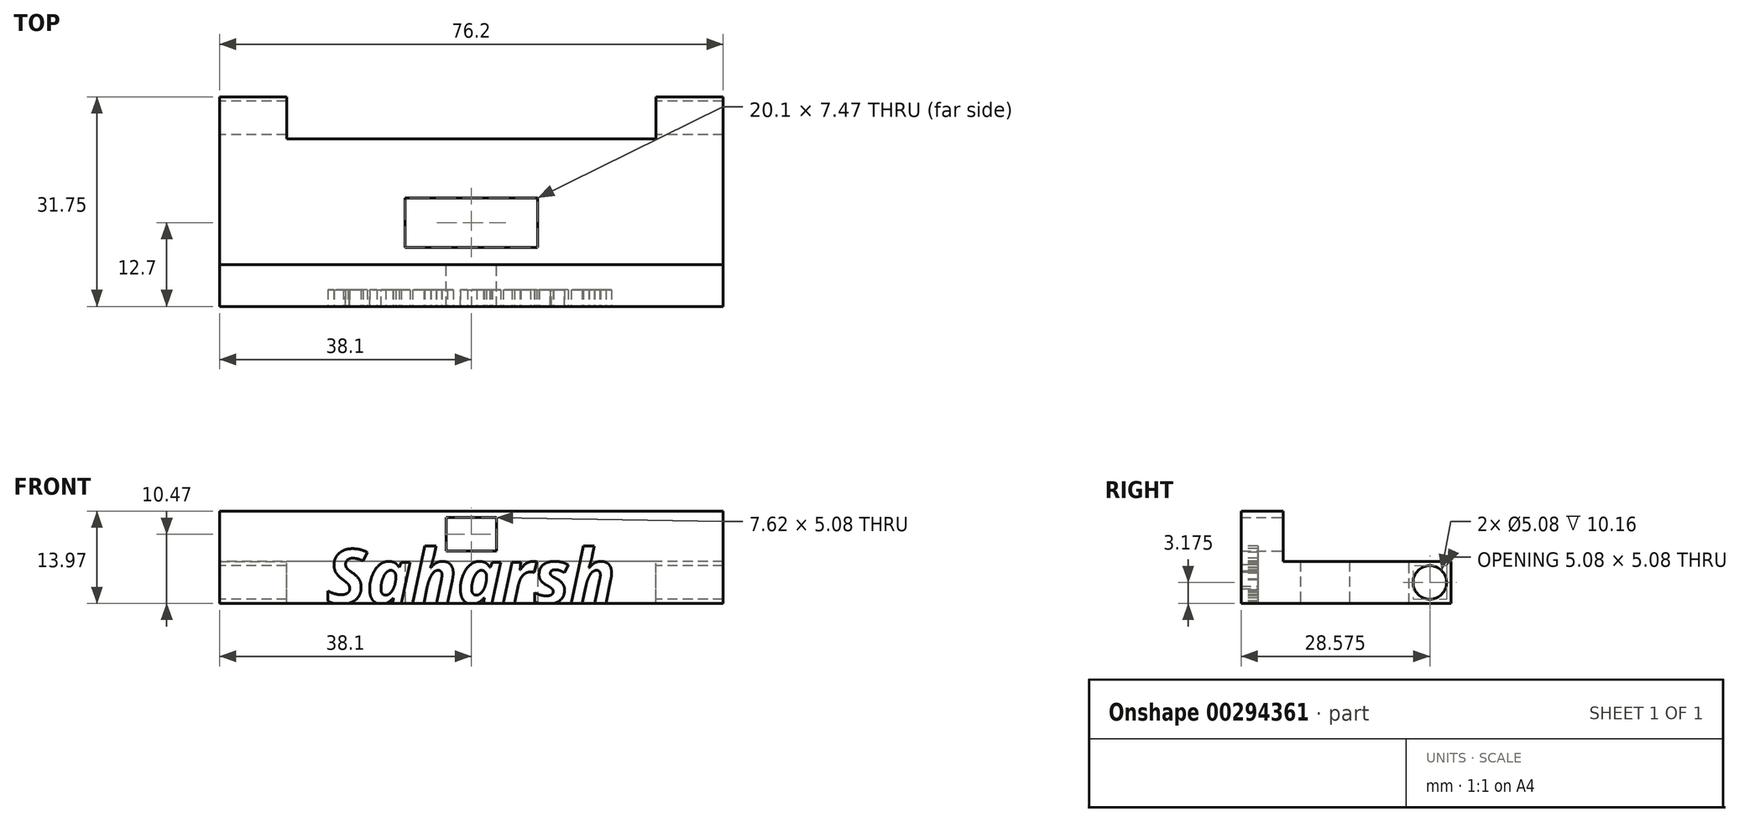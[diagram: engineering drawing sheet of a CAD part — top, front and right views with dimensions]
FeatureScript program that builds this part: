
annotation { "Feature Type Name" : "Feature", "Feature Type Description" : "" }
export const myFeature = defineFeature(function(context is Context, id is Id, definition is map)
    precondition{}
    {
        {
            var Q0;
            Q0=qCreatedBy(makeId("Top.planeOp"),FACE);
            var sketch = newSketch(context, id + "F0", { "sketchPlane" : qUnion([Q0])});
            skLineSegment(sketch, "E0.bottom", {"start": v(38.1, -12.7) * mm, "end": v(-38.1, -12.7) * mm});
            skLineSegment(sketch, "E0.top", {"start": v(38.1, 12.7) * mm, "end": v(-38.1, 12.7) * mm});
            skLineSegment(sketch, "E0.left", {"start": v(38.1, -12.7) * mm, "end": v(38.1, 12.7) * mm});
            skLineSegment(sketch, "E0.right", {"start": v(-38.1, -12.7) * mm, "end": v(-38.1, 12.7) * mm});
            skPoint(sketch, "E0.middle", {"position": v(0, 0) * mm});
            skSolve(sketch);
        }
        {
            var Q0;
            Q0=qCreatedBy(makeId("Top.planeOp"),FACE);
            var sketch = newSketch(context, id + "F1", { "sketchPlane" : qUnion([Q0])});
            skLineSegment(sketch, "E1.bottom", {"start": v(10.05, -3.74) * mm, "end": v(-10.05, -3.74) * mm});
            skLineSegment(sketch, "E1.top", {"start": v(10.05, 3.74) * mm, "end": v(-10.05, 3.74) * mm});
            skLineSegment(sketch, "E1.left", {"start": v(10.05, -3.74) * mm, "end": v(10.05, 3.74) * mm});
            skLineSegment(sketch, "E1.right", {"start": v(-10.05, -3.74) * mm, "end": v(-10.05, 3.74) * mm});
            skPoint(sketch, "E1.middle", {"position": v(0, 0) * mm});
            skSolve(sketch);
        }
        {
            var Q0;
            Q0=makeQuery(id+"F0.imprint","IMPRINT",FACE,{"disambiguationData":[TD([[makeQuery(id+"F0.imprint","IMPRINT",EDGE,{"derivedFrom":sQuery(id+"F0.wireOp",EDGE,"E0.bottom")}),-1.0]])]});
            extrude(context, id + "F2", {"entities" : qUnion([Q0]), "depth" : 6.35 * mm});
        }
        {
            var Q0;
            Q0=qSketchRegion(id+"F1",true);
            extrude(context, id + "F3", {"entities" : qUnion([Q0]), "operationType" : NewBodyOperationType.REMOVE, "depth" : 6.35 * mm});
        }
        {
            var Q0;
            Q0=qCreatedBy(makeId("Front.planeOp"),FACE);
            var sketch = newSketch(context, id + "F4", { "sketchPlane" : qUnion([Q0])});
            skLineSegment(sketch, "E2.bottom", {"start": v(38.1, 0) * mm, "end": v(27.94, 0) * mm});
            skLineSegment(sketch, "E2.top", {"start": v(38.1, 6.35) * mm, "end": v(27.94, 6.35) * mm});
            skLineSegment(sketch, "E2.left", {"start": v(38.1, 0) * mm, "end": v(38.1, 6.35) * mm});
            skLineSegment(sketch, "E2.right", {"start": v(27.94, 0) * mm, "end": v(27.94, 6.35) * mm});
            skLineSegment(sketch, "E3.MirrorCS", {"start": v(-27.94, 0) * mm, "end": v(-27.94, 6.35) * mm});
            skLineSegment(sketch, "E4.MirrorCS", {"start": v(-38.1, 0) * mm, "end": v(-38.1, 6.35) * mm});
            skLineSegment(sketch, "E5.MirrorCS", {"start": v(-38.1, 6.35) * mm, "end": v(-27.94, 6.35) * mm});
            skLineSegment(sketch, "E6.MirrorCS", {"start": v(-38.1, 0) * mm, "end": v(-27.94, 0) * mm});
            skSolve(sketch);
        }
        {
            var Q0;
            Q0=qSketchRegion(id+"F4",true);
            extrude(context, id + "F5", {"entities" : qUnion([Q0]), "operationType" : NewBodyOperationType.ADD, "oppositeDirection" : true, "depth" : 19.05 * mm});
        }
        {
            var Q0;
            Q0=makeQuery(id+"F5.boolean.opBoolean","MERGE",FACE,{"derivedFrom":[makeQuery(id+"F2.opExtrude","SWEPT_FACE",FACE,{"disambiguationData":[OSD([sQuery(id+"F0.wireOp",EDGE,"E0.right")])]}),makeQuery(id+"F5.opExtrude","SWEPT_FACE",FACE,{"disambiguationData":[OSD([sQuery(id+"F4.wireOp",EDGE,"E4.MirrorCS")])]})]});
            var sketch = newSketch(context, id + "F6", { "sketchPlane" : qUnion([Q0])});
            skCircle(sketch, "E7", {"center": v(-15.87, 3.17) * mm, "radius": 2.54 * mm});
            skPoint(sketch, "E8", {"position": v(-19.05, 3.17) * mm});
            skCircle(sketch, "E9", {"center": v(-15.87, 3.17) * mm, "radius": 3.18 * mm});
            skSolve(sketch);
        }
        {
            var Q0;
            Q0=makeQuery(id+"F6.imprint","IMPRINT",FACE,{"disambiguationData":[TD([[makeQuery(id+"F6.imprint","IMPRINT",EDGE,{"derivedFrom":sQuery(id+"F6.wireOp",EDGE,"E7")}),1.0]])]});
            extrude(context, id + "F7", {"entities" : qUnion([Q0]), "operationType" : NewBodyOperationType.REMOVE, "oppositeDirection" : true, "depth" : 76.2 * mm});
        }
        {
            var Q0;
            Q0=qCreatedBy(makeId("Top.planeOp"),FACE);
            var sketch = newSketch(context, id + "F8", { "sketchPlane" : qUnion([Q0])});
            skLineSegment(sketch, "E10.bottom", {"start": v(-38.1, -12.7) * mm, "end": v(38.1, -12.7) * mm});
            skLineSegment(sketch, "E10.top", {"start": v(-38.1, -6.35) * mm, "end": v(38.1, -6.35) * mm});
            skLineSegment(sketch, "E10.left", {"start": v(-38.1, -12.7) * mm, "end": v(-38.1, -6.35) * mm});
            skLineSegment(sketch, "E10.right", {"start": v(38.1, -12.7) * mm, "end": v(38.1, -6.35) * mm});
            skSolve(sketch);
        }
        {
            var Q0;
            Q0=qSketchRegion(id+"F8",true);
            extrude(context, id + "F9", {"entities" : qUnion([Q0]), "operationType" : NewBodyOperationType.ADD, "depth" : 13.97 * mm});
        }
        {
            var Q0;
            Q0=makeQuery(id+"F9.boolean.opBoolean","MERGE",FACE,{"derivedFrom":[makeQuery(id+"F2.opExtrude","SWEPT_FACE",FACE,{"disambiguationData":[OSD([sQuery(id+"F0.wireOp",EDGE,"E0.bottom")])]}),makeQuery(id+"F9.opExtrude","SWEPT_FACE",FACE,{"disambiguationData":[OSD([sQuery(id+"F8.wireOp",EDGE,"E10.bottom")])]})]});
            var sketch = newSketch(context, id + "F10", { "sketchPlane" : qUnion([Q0])});
            skLineSegment(sketch, "E11.right", {"start": v(55.82, 5.12) * mm, "end": v(55.82, 5.12) * mm});
            skLineSegment(sketch, "E12.bottom", {"start": v(-3.81, 7.93) * mm, "end": v(3.81, 7.93) * mm});
            skLineSegment(sketch, "E12.top", {"start": v(-3.81, 13.01) * mm, "end": v(3.8, 13.01) * mm});
            skLineSegment(sketch, "E12.left", {"start": v(-3.81, 7.93) * mm, "end": v(-3.81, 13.01) * mm});
            skLineSegment(sketch, "E12.right", {"start": v(3.81, 7.93) * mm, "end": v(3.8, 13.01) * mm});
            skPoint(sketch, "E12.middle", {"position": v(0, 10.47) * mm});
            skSolve(sketch);
        }
        {
            var Q0;
            Q0=qSketchRegion(id+"F10",true);
            extrude(context, id + "F11", {"entities" : qUnion([Q0]), "operationType" : NewBodyOperationType.ADD, "depth" : 25.4 * mm});
        }
        {
            var Q0;
            Q0=makeQuery(id+"F11.opExtrude","CAP_FACE",FACE,{"disambiguationData":[OSD([sQuery(id+"F10.wireOp",EDGE,"E12.bottom"),sQuery(id+"F10.wireOp",EDGE,"E12.top"),sQuery(id+"F10.wireOp",EDGE,"E12.left"),sQuery(id+"F10.wireOp",EDGE,"E12.right")])],"isStart":false});
            extrude(context, id + "F12", {"entities" : qUnion([Q0]), "operationType" : NewBodyOperationType.REMOVE, "endBound" : BoundingType.SYMMETRIC, "depth" : 381 * mm});
        }
        {
            var Q0;
            Q0=makeQuery(id+"F9.boolean.opBoolean","MERGE",FACE,{"derivedFrom":[makeQuery(id+"F2.opExtrude","SWEPT_FACE",FACE,{"disambiguationData":[OSD([sQuery(id+"F0.wireOp",EDGE,"E0.bottom")])]}),makeQuery(id+"F9.opExtrude","SWEPT_FACE",FACE,{"disambiguationData":[OSD([sQuery(id+"F8.wireOp",EDGE,"E10.bottom")])]})]});
            var sketch = newSketch(context, id + "F13", { "sketchPlane" : qUnion([Q0])});
            skText(sketch, "E13", { "text": "Saharsh", "fontName": "NotoSans-BoldItalic.ttf"});
            const initialGuessF13  = {"E13": [-0.02196, 0, 1, 0, 0.00825]};
            skSetInitialGuess(sketch, initialGuessF13);
            skSolve(sketch);
        }
        {
            var Q0;
            Q0 = qSketchRegion(id + "F13", true);
            extrude(context, id + "F14", {"entities" : qUnion([Q0]), "operationType" : NewBodyOperationType.REMOVE, "oppositeDirection" : true, "depth" : 2.54 * mm});
        }
    });
